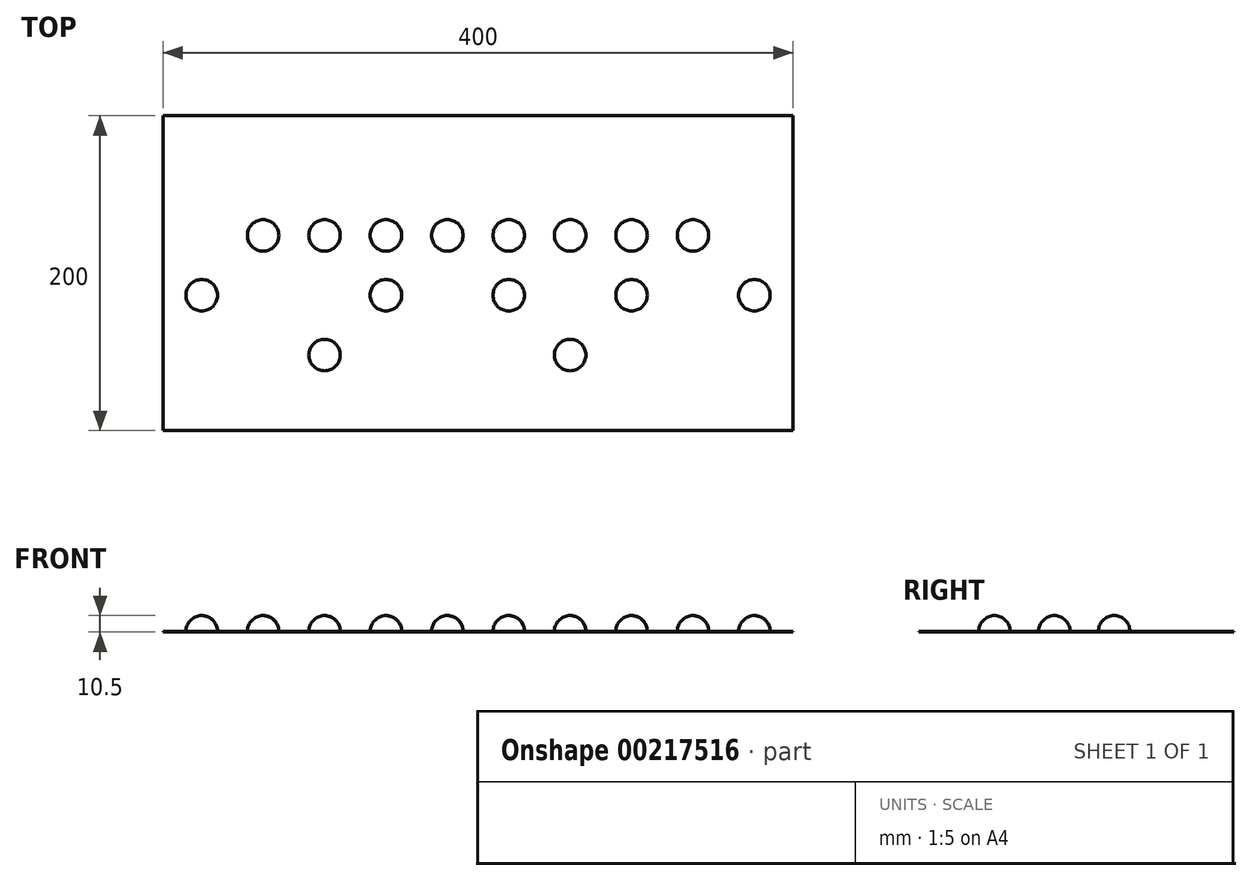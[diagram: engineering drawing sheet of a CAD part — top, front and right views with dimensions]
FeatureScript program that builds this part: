
annotation { "Feature Type Name" : "Feature", "Feature Type Description" : "" }
export const myFeature = defineFeature(function(context is Context, id is Id, definition is map)
    precondition{}
    {
        {
            var Q0;
            Q0=qCreatedBy(makeId("Top.planeOp"),FACE);
            var sketch = newSketch(context, id + "F0", { "sketchPlane" : qUnion([Q0])});
            skLineSegment(sketch, "E0.bottom", {"start": v(0, 0) * mm, "end": v(400, 0) * mm});
            skLineSegment(sketch, "E0.top", {"start": v(0, 200) * mm, "end": v(400, 200) * mm});
            skLineSegment(sketch, "E0.left", {"start": v(0, 0) * mm, "end": v(0, 200) * mm});
            skLineSegment(sketch, "E0.right", {"start": v(400, 0) * mm, "end": v(400, 200) * mm});
            skSolve(sketch);
        }
        {
            var Q0;
            Q0 = qSketchRegion(id + "F0", true);
            extrude(context, id + "F1", {"entities" : qUnion([Q0]), "depth" : 0.5 * mm});
        }
        {
            var Q0;
            Q0=qCreatedBy(makeId("Top.planeOp"),FACE);
            var sketch = newSketch(context, id + "F2", { "sketchPlane" : qUnion([Q0])});
            skSolve(sketch);
        }
        {
            var Q0;
            Q0=makeQuery(id+"F1.opExtrude","CAP_FACE",FACE,{"disambiguationData":[OSD([sQuery(id+"F0.wireOp",EDGE,"E0.bottom"),sQuery(id+"F0.wireOp",EDGE,"E0.top"),sQuery(id+"F0.wireOp",EDGE,"E0.left"),sQuery(id+"F0.wireOp",EDGE,"E0.right")])],"isStart":false});
            var sketch = newSketch(context, id + "F3", { "sketchPlane" : qUnion([Q0])});
            skCircle(sketch, "E1", {"center": v(24.5, 48) * mm, "radius": 10 * mm});
            skCircle(sketch, "E2.0.1.0", {"center": v(24.5, 86) * mm, "radius": 10 * mm});
            skCircle(sketch, "E2.0.2.0", {"center": v(24.5, 124) * mm, "radius": 10 * mm});
            skCircle(sketch, "E2.1.0.0", {"center": v(63.5, 48) * mm, "radius": 10 * mm});
            skCircle(sketch, "E2.1.1.0", {"center": v(63.5, 86) * mm, "radius": 10 * mm});
            skCircle(sketch, "E2.1.2.0", {"center": v(63.5, 124) * mm, "radius": 10 * mm});
            skCircle(sketch, "E2.2.0.0", {"center": v(102.5, 48) * mm, "radius": 10 * mm});
            skCircle(sketch, "E2.2.1.0", {"center": v(102.5, 86) * mm, "radius": 10 * mm});
            skCircle(sketch, "E2.2.2.0", {"center": v(102.5, 124) * mm, "radius": 10 * mm});
            skCircle(sketch, "E2.3.0.0", {"center": v(141.5, 48) * mm, "radius": 10 * mm});
            skCircle(sketch, "E2.3.1.0", {"center": v(141.5, 86) * mm, "radius": 10 * mm});
            skCircle(sketch, "E2.3.2.0", {"center": v(141.5, 124) * mm, "radius": 10 * mm});
            skCircle(sketch, "E2.4.0.0", {"center": v(180.5, 48) * mm, "radius": 10 * mm});
            skCircle(sketch, "E2.4.1.0", {"center": v(180.5, 86) * mm, "radius": 10 * mm});
            skCircle(sketch, "E2.4.2.0", {"center": v(180.5, 124) * mm, "radius": 10 * mm});
            skCircle(sketch, "E2.5.0.0", {"center": v(219.5, 48) * mm, "radius": 10 * mm});
            skCircle(sketch, "E2.5.1.0", {"center": v(219.5, 86) * mm, "radius": 10 * mm});
            skCircle(sketch, "E2.5.2.0", {"center": v(219.5, 124) * mm, "radius": 10 * mm});
            skCircle(sketch, "E2.6.0.0", {"center": v(258.5, 48) * mm, "radius": 10 * mm});
            skCircle(sketch, "E2.6.1.0", {"center": v(258.5, 86) * mm, "radius": 10 * mm});
            skCircle(sketch, "E2.6.2.0", {"center": v(258.5, 124) * mm, "radius": 10 * mm});
            skCircle(sketch, "E2.7.0.0", {"center": v(297.5, 48) * mm, "radius": 10 * mm});
            skCircle(sketch, "E2.7.1.0", {"center": v(297.5, 86) * mm, "radius": 10 * mm});
            skCircle(sketch, "E2.7.2.0", {"center": v(297.5, 124) * mm, "radius": 10 * mm});
            skCircle(sketch, "E2.8.0.0", {"center": v(336.5, 48) * mm, "radius": 10 * mm});
            skCircle(sketch, "E2.8.1.0", {"center": v(336.5, 86) * mm, "radius": 10 * mm});
            skCircle(sketch, "E2.8.2.0", {"center": v(336.5, 124) * mm, "radius": 10 * mm});
            skCircle(sketch, "E2.9.0.0", {"center": v(375.5, 48) * mm, "radius": 10 * mm});
            skCircle(sketch, "E2.9.1.0", {"center": v(375.5, 86) * mm, "radius": 10 * mm});
            skCircle(sketch, "E2.9.2.0", {"center": v(375.5, 124) * mm, "radius": 10 * mm});
            skLineSegment(sketch, "E2.direction1", {"start": v(24.5, 48) * mm, "end": v(63.5, 48) * mm, "construction": true});
            skLineSegment(sketch, "E2.direction2", {"start": v(24.5, 48) * mm, "end": v(24.5, 86) * mm, "construction": true});
            skSolve(sketch);
        }
        {
            var Q0;
            Q0 = qSketchRegion(id + "F3", true);
            extrude(context, id + "F4", {"entities" : qUnion([Q0]), "depth" : 10 * mm});
        }
        {
            var Q0;
            Q0=makeQuery(id+"F4.opExtrude","SWEPT_BODY",BODY,{"disambiguationData":[OSD([sQuery(id+"F3.wireOp",EDGE,"E2.1.1.0")])]});
            var Q1;
            Q1=makeQuery(id+"F4.opExtrude","SWEPT_BODY",BODY,{"disambiguationData":[OSD([sQuery(id+"F3.wireOp",EDGE,"E2.0.2.0")])]});
            var Q2;
            Q2=makeQuery(id+"F4.opExtrude","SWEPT_BODY",BODY,{"disambiguationData":[OSD([sQuery(id+"F3.wireOp",EDGE,"E2.2.1.0")])]});
            var Q3;
            Q3=makeQuery(id+"F4.opExtrude","SWEPT_BODY",BODY,{"disambiguationData":[OSD([sQuery(id+"F3.wireOp",EDGE,"E2.1.0.0")])]});
            var Q4;
            Q4=makeQuery(id+"F4.opExtrude","SWEPT_BODY",BODY,{"disambiguationData":[OSD([sQuery(id+"F3.wireOp",EDGE,"E1")])]});
            var Q5;
            Q5=makeQuery(id+"F4.opExtrude","SWEPT_BODY",BODY,{"disambiguationData":[OSD([sQuery(id+"F3.wireOp",EDGE,"E2.3.0.0")])]});
            var Q6;
            Q6=makeQuery(id+"F4.opExtrude","SWEPT_BODY",BODY,{"disambiguationData":[OSD([sQuery(id+"F3.wireOp",EDGE,"E2.4.0.0")])]});
            var Q7;
            Q7=makeQuery(id+"F4.opExtrude","SWEPT_BODY",BODY,{"disambiguationData":[OSD([sQuery(id+"F3.wireOp",EDGE,"E2.4.1.0")])]});
            var Q8;
            Q8=makeQuery(id+"F4.opExtrude","SWEPT_BODY",BODY,{"disambiguationData":[OSD([sQuery(id+"F3.wireOp",EDGE,"E2.5.0.0")])]});
            var Q9;
            Q9=makeQuery(id+"F4.opExtrude","SWEPT_BODY",BODY,{"disambiguationData":[OSD([sQuery(id+"F3.wireOp",EDGE,"E2.6.1.0")])]});
            var Q10;
            Q10=makeQuery(id+"F4.opExtrude","SWEPT_BODY",BODY,{"disambiguationData":[OSD([sQuery(id+"F3.wireOp",EDGE,"E2.8.1.0")])]});
            var Q11;
            Q11=makeQuery(id+"F4.opExtrude","SWEPT_BODY",BODY,{"disambiguationData":[OSD([sQuery(id+"F3.wireOp",EDGE,"E2.8.0.0")])]});
            var Q12;
            Q12=makeQuery(id+"F4.opExtrude","SWEPT_BODY",BODY,{"disambiguationData":[OSD([sQuery(id+"F3.wireOp",EDGE,"E2.7.0.0")])]});
            var Q13;
            Q13=makeQuery(id+"F4.opExtrude","SWEPT_BODY",BODY,{"disambiguationData":[OSD([sQuery(id+"F3.wireOp",EDGE,"E2.9.0.0")])]});
            var Q14;
            Q14=makeQuery(id+"F4.opExtrude","SWEPT_BODY",BODY,{"disambiguationData":[OSD([sQuery(id+"F3.wireOp",EDGE,"E2.9.2.0")])]});
            deleteBodies(context, id + "F5", {"entities" : qUnion([Q0, Q1, Q2, Q3, Q4, Q5, Q6, Q7, Q8, Q9, Q10, Q11, Q12, Q13, Q14])});
        }
        {
            var Q0;
            Q0=makeQuery(id+"F4.opExtrude","CAP_EDGE",EDGE,{"disambiguationData":[OSD([sQuery(id+"F3.wireOp",EDGE,"E2.0.1.0")])],"isStart":false});
            var Q1;
            Q1=makeQuery(id+"F4.opExtrude","CAP_EDGE",EDGE,{"disambiguationData":[OSD([sQuery(id+"F3.wireOp",EDGE,"E2.1.2.0")])],"isStart":false});
            var Q2;
            Q2=makeQuery(id+"F4.opExtrude","CAP_EDGE",EDGE,{"disambiguationData":[OSD([sQuery(id+"F3.wireOp",EDGE,"E2.2.2.0")])],"isStart":false});
            var Q3;
            Q3=makeQuery(id+"F4.opExtrude","CAP_EDGE",EDGE,{"disambiguationData":[OSD([sQuery(id+"F3.wireOp",EDGE,"E2.3.2.0")])],"isStart":false});
            var Q4;
            Q4=makeQuery(id+"F4.opExtrude","CAP_EDGE",EDGE,{"disambiguationData":[OSD([sQuery(id+"F3.wireOp",EDGE,"E2.3.1.0")])],"isStart":false});
            var Q5;
            Q5=makeQuery(id+"F4.opExtrude","CAP_EDGE",EDGE,{"disambiguationData":[OSD([sQuery(id+"F3.wireOp",EDGE,"E2.2.0.0")])],"isStart":false});
            var Q6;
            Q6=makeQuery(id+"F4.opExtrude","CAP_EDGE",EDGE,{"disambiguationData":[OSD([sQuery(id+"F3.wireOp",EDGE,"E2.4.2.0")])],"isStart":false});
            var Q7;
            Q7=makeQuery(id+"F4.opExtrude","CAP_EDGE",EDGE,{"disambiguationData":[OSD([sQuery(id+"F3.wireOp",EDGE,"E2.5.2.0")])],"isStart":false});
            var Q8;
            Q8=makeQuery(id+"F4.opExtrude","CAP_EDGE",EDGE,{"disambiguationData":[OSD([sQuery(id+"F3.wireOp",EDGE,"E2.5.1.0")])],"isStart":false});
            var Q9;
            Q9=makeQuery(id+"F4.opExtrude","CAP_EDGE",EDGE,{"disambiguationData":[OSD([sQuery(id+"F3.wireOp",EDGE,"E2.6.2.0")])],"isStart":false});
            var Q10;
            Q10=makeQuery(id+"F4.opExtrude","CAP_EDGE",EDGE,{"disambiguationData":[OSD([sQuery(id+"F3.wireOp",EDGE,"E2.7.2.0")])],"isStart":false});
            var Q11;
            Q11=makeQuery(id+"F4.opExtrude","CAP_EDGE",EDGE,{"disambiguationData":[OSD([sQuery(id+"F3.wireOp",EDGE,"E2.8.2.0")])],"isStart":false});
            var Q12;
            Q12=makeQuery(id+"F4.opExtrude","CAP_EDGE",EDGE,{"disambiguationData":[OSD([sQuery(id+"F3.wireOp",EDGE,"E2.9.1.0")])],"isStart":false});
            var Q13;
            Q13=makeQuery(id+"F4.opExtrude","CAP_EDGE",EDGE,{"disambiguationData":[OSD([sQuery(id+"F3.wireOp",EDGE,"E2.7.1.0")])],"isStart":false});
            var Q14;
            Q14=makeQuery(id+"F4.opExtrude","CAP_EDGE",EDGE,{"disambiguationData":[OSD([sQuery(id+"F3.wireOp",EDGE,"E2.6.0.0")])],"isStart":false});
            fillet(context, id + "F6", {"entities" : qUnion([Q0, Q1, Q2, Q3, Q4, Q5, Q6, Q7, Q8, Q9, Q10, Q11, Q12, Q13, Q14]), "radius" : 10 * mm, "tangentPropagation" : true, "allowEdgeOverflow" : false});
        }
    });
